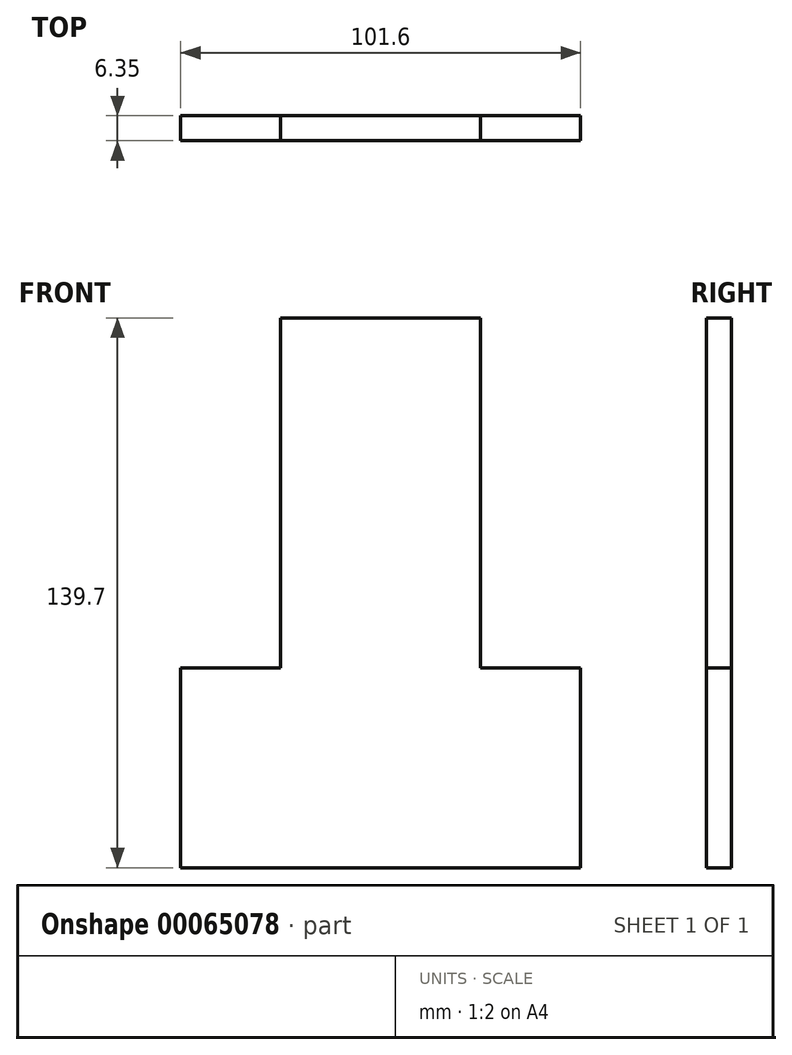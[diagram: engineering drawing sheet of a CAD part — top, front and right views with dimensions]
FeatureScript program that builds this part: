
annotation { "Feature Type Name" : "Feature", "Feature Type Description" : "" }
export const myFeature = defineFeature(function(context is Context, id is Id, definition is map)
    precondition{}
    {
        {
            var Q0;
            Q0=qCreatedBy(makeId("Front.planeOp"),FACE);
            var sketch = newSketch(context, id + "F0", { "sketchPlane" : qUnion([Q0])});
            skLineSegment(sketch, "E0.bottom", {"start": v(-25.4, 69.85) * mm, "end": v(25.4, 69.85) * mm});
            skLineSegment(sketch, "E0.top", {"start": v(-25.4, -69.85) * mm, "end": v(25.4, -69.85) * mm});
            skLineSegment(sketch, "E0.left", {"start": v(-25.4, 69.85) * mm, "end": v(-25.4, -69.85) * mm});
            skLineSegment(sketch, "E0.right", {"start": v(25.4, 69.85) * mm, "end": v(25.4, -69.85) * mm});
            skPoint(sketch, "E0.middle", {"position": v(0, 0) * mm});
            skLineSegment(sketch, "E1.bottom", {"start": v(25.4, -69.85) * mm, "end": v(50.8, -69.85) * mm});
            skLineSegment(sketch, "E1.top", {"start": v(25.4, -19.05) * mm, "end": v(50.8, -19.05) * mm});
            skLineSegment(sketch, "E1.left", {"start": v(25.4, -69.85) * mm, "end": v(25.4, -19.05) * mm});
            skLineSegment(sketch, "E1.right", {"start": v(50.8, -69.85) * mm, "end": v(50.8, -19.05) * mm});
            skLineSegment(sketch, "E2.bottom", {"start": v(-25.4, -69.85) * mm, "end": v(-50.8, -69.85) * mm});
            skLineSegment(sketch, "E2.top", {"start": v(-25.4, -19.05) * mm, "end": v(-50.8, -19.05) * mm});
            skLineSegment(sketch, "E2.left", {"start": v(-25.4, -69.85) * mm, "end": v(-25.4, -19.05) * mm});
            skLineSegment(sketch, "E2.right", {"start": v(-50.8, -69.85) * mm, "end": v(-50.8, -19.05) * mm});
            skSolve(sketch);
        }
        {
            var Q0;
            Q0 = qSketchRegion(id + "F0", true);
            extrude(context, id + "F1", {"entities" : qUnion([Q0]), "depth" : 6.35 * mm});
        }
    });
